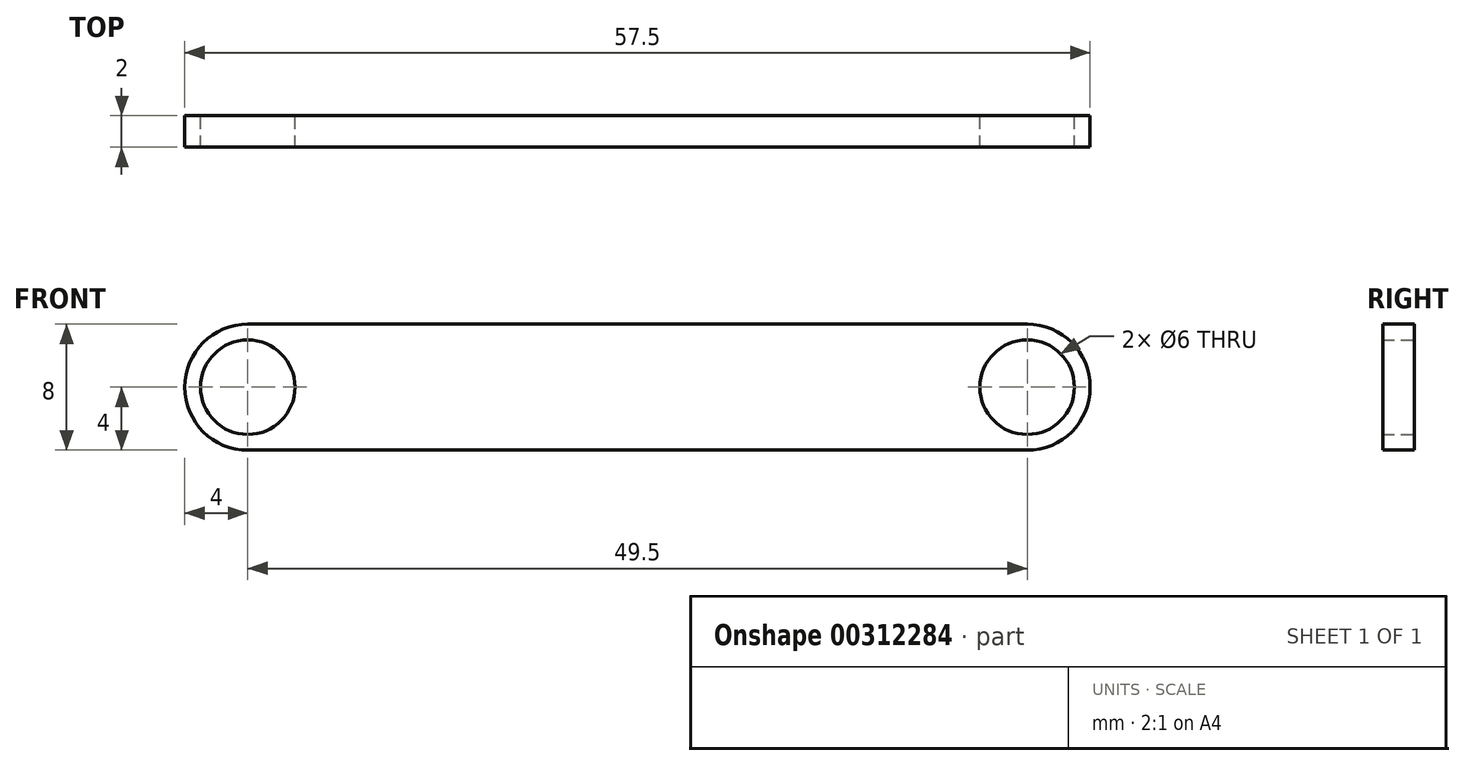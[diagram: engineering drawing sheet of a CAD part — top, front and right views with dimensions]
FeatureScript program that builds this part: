
annotation { "Feature Type Name" : "Feature", "Feature Type Description" : "" }
export const myFeature = defineFeature(function(context is Context, id is Id, definition is map)
    precondition{}
    {
        {
            var Q0;
            Q0=qCreatedBy(makeId("Front.planeOp"),FACE);
            var sketch = newSketch(context, id + "F0", { "sketchPlane" : qUnion([Q0])});
            skCircle(sketch, "E0", {"center": v(-24.75, 0) * mm, "radius": 3 * mm});
            skCircle(sketch, "E1", {"center": v(24.75, 0) * mm, "radius": 3 * mm});
            skArc(sketch, "E2", {"start": v(-24.75, 4) * mm, "mid": v(-28.75, 0) * mm, "end": v(-24.75, -4) * mm});
            skArc(sketch, "E3", {"start": v(24.75, -4) * mm, "mid": v(28.75, 0) * mm, "end": v(24.75, 4) * mm});
            skLineSegment(sketch, "E4", {"start": v(-24.75, 4) * mm, "end": v(24.75, 4) * mm});
            skLineSegment(sketch, "E5", {"start": v(-24.75, -4) * mm, "end": v(24.75, -4) * mm});
            skSolve(sketch);
        }
        {
            var Q0;
            Q0=qSketchRegion(id+"F0",true);
            extrude(context, id + "F1", {"entities" : qUnion([Q0]), "depth" : 2 * mm});
        }
    });
